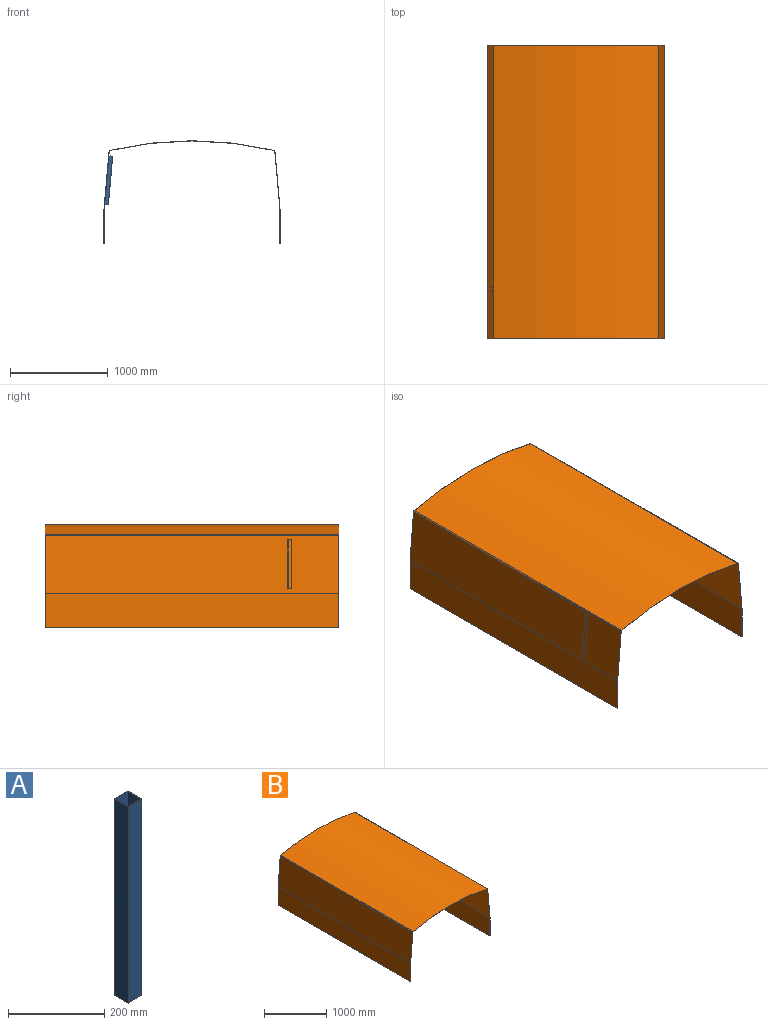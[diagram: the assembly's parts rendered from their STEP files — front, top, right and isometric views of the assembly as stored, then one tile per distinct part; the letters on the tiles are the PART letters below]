
ASSEMBLY  parts=2 mates=1
PART A: 10 faces, bbox 40x40x500 mm
  f0: plane 500x37mm, normal (-1,0,0), area 18500mm2, adj f1,f7,f8,f9
  f1: plane 500x37mm, normal (0,1,0), area 18500mm2, adj f0,f2,f8,f9
  f2: plane 500x37mm, normal (1,0,0), area 18500mm2, adj f1,f7,f8,f9
  f3: plane 500x40mm, normal (0,-1,0), area 20000mm2, adj f4,f6,f8,f9
  f4: plane 500x40mm, normal (1,0,0), area 20000mm2, adj f3,f5,f8,f9
  f5: plane 500x40mm, normal (0,1,0), area 20000mm2, adj f4,f6,f8,f9
  f6: plane 500x40mm, normal (-1,0,0), area 20000mm2, adj f3,f5,f8,f9
  f7: plane 500x37mm, normal (0,-1,0), area 18500mm2, adj f0,f2,f8,f9
  f8: plane 40x40mm, normal (0,0,1), area 231mm2, adj f0,f1,f2,f3,f4,f5,f6,f7
  f9: plane 40x40mm, normal (0,0,-1), area 231mm2, adj f0,f1,f2,f3,f4,f5,f6,f7
PART B: 18 faces, bbox 1800x3000x1047.7 mm
  f0: plane 3000x2mm, normal (0,0,-1), area 6000mm2, adj f1,f11,f12,f13
  f1: plane 3000x349.91mm, normal (1,0,0), area 1049738mm2, adj f0,f2,f12,f13
  f2: plane 3000x589.01mm, normal (1,0,-0.09), area 1773768.1mm2, adj f1,f12,f13,f14
  f3: cylinder r=3641.03mm len=3000mm, axis (0,1,0), area 5078479.6mm2, adj f12,f13,f14,f17
  f4: plane 3000x589.01mm, normal (-1,0,-0.09), area 1773768.1mm2, adj f5,f12,f13,f17
  f5: plane 3000x349.91mm, normal (-1,0,0), area 1049738mm2, adj f4,f6,f12,f13
  f6: plane 3000x2mm, normal (0,0,-1), area 6000mm2, adj f5,f7,f12,f13
  f7: plane 3000x350mm, normal (1,0,0), area 1050000mm2, adj f6,f8,f12,f13
  f8: plane 3000x590.53mm, normal (1,0,0.09), area 1778362.9mm2, adj f7,f12,f13,f16
  f9: cylinder r=3643.03mm len=3000mm, axis (0,1,0), area 5089961.1mm2, adj f12,f13,f15,f16
  f10: plane 3000x590.53mm, normal (-1,0,0.09), area 1778362.9mm2, adj f11,f12,f13,f15
  f11: plane 3000x350mm, normal (-1,0,0), area 1050000mm2, adj f0,f10,f12,f13
  f12: plane 1800x1047.72mm, normal (0,-1,0), area 7215.2mm2, adj f0,f1,f2,f3,f4,f5,f6,f7
  f13: plane 1800x1047.72mm, normal (0,1,0), area 7215.2mm2, adj f0,f1,f2,f3,f4,f5,f6,f7
  f14: cylinder r=10mm len=3000mm, axis (0,1,0), area 37531.9mm2, adj f2,f3,f12,f13
  f15: cylinder r=10mm len=3000mm, axis (0,1,0), area 37520mm2, adj f9,f10,f12,f13
  f16: cylinder r=10mm len=3000mm, axis (0,1,0), area 37520mm2, adj f8,f9,f12,f13
  f17: cylinder r=10mm len=3000mm, axis (0,1,0), area 37531.9mm2, adj f3,f4,f12,f13
PLACE A rot(axis=(-0.04,0.04,-1),90.1deg) t=(-874.1,-1000,393.62)mm
PLACE B at identity fixed
MATE fastened B.f2 <-> A.f3  axis (1,0,-0.09) through (-872.23,0,644.42)mm
